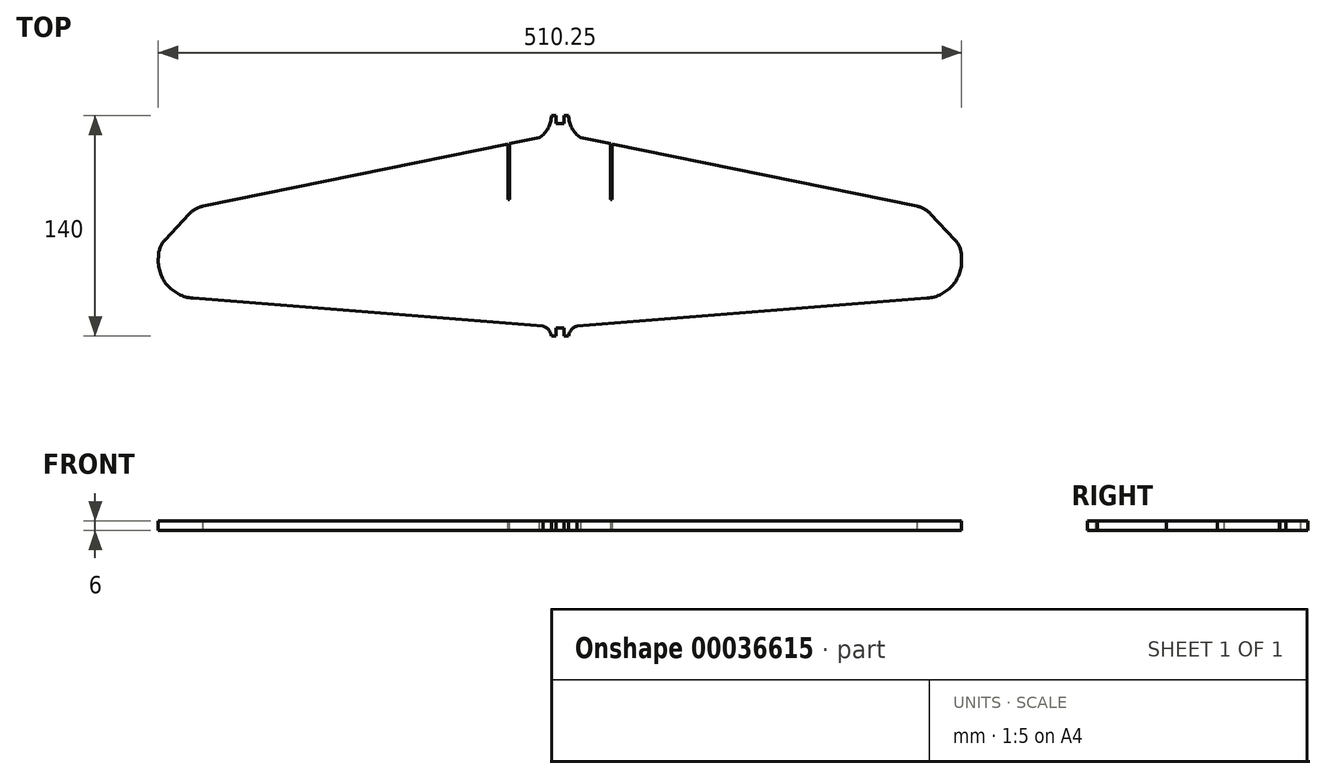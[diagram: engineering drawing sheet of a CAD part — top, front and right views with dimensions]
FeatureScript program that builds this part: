
annotation { "Feature Type Name" : "Feature", "Feature Type Description" : "" }
export const myFeature = defineFeature(function(context is Context, id is Id, definition is map)
    precondition{}
    {
        {
            var Q0;
            Q0=qCreatedBy(makeId("Top.planeOp"),FACE);
            var sketch = newSketch(context, id + "F0", { "sketchPlane" : qUnion([Q0])});
            skLineSegment(sketch, "E0", {"start": v(-57.17, -18.86) * mm, "end": v(-57.17, -69.04) * mm});
            skLineSegment(sketch, "E1", {"start": v(-57.17, -18.86) * mm, "end": v(-57.17, 70.96) * mm});
            skLineSegment(sketch, "E2", {"start": v(-51.78, -62.82) * mm, "end": v(170.5, -45.05) * mm});
            skArc(sketch, "E3", {"start": v(-51.78, -62.82) * mm, "mid": v(-55.43, -65.1) * mm, "end": v(-57.17, -69.04) * mm});
            skArc(sketch, "E4", {"start": v(170.5, -45.05) * mm, "mid": v(186.92, -36.55) * mm, "end": v(192.33, -18.86) * mm});
            skLineSegment(sketch, "E5", {"start": v(-49.68, 56.96) * mm, "end": v(163.94, 13.41) * mm});
            skLineSegment(sketch, "E6", {"start": v(172.75, 8.43) * mm, "end": v(188.16, -7.97) * mm});
            skArc(sketch, "E7", {"start": v(172.75, 8.43) * mm, "mid": v(168.72, 11.59) * mm, "end": v(163.94, 13.41) * mm});
            skArc(sketch, "E8", {"start": v(192.33, -18.86) * mm, "mid": v(191.32, -13) * mm, "end": v(188.16, -7.97) * mm});
            skArc(sketch, "E9", {"start": v(-57.17, 70.96) * mm, "mid": v(-55.18, 63.02) * mm, "end": v(-49.68, 56.96) * mm});
            skLineSegment(sketch, "E10.bottom", {"start": v(-57.17, 70.96) * mm, "end": v(-60.17, 70.96) * mm});
            skLineSegment(sketch, "E10.top", {"start": v(-57.17, -69.04) * mm, "end": v(-60.17, -69.04) * mm});
            skLineSegment(sketch, "E10.left", {"start": v(-57.17, 70.96) * mm, "end": v(-57.17, -69.04) * mm});
            skLineSegment(sketch, "E11", {"start": v(-60.17, 70.96) * mm, "end": v(-60.17, 65.96) * mm});
            skLineSegment(sketch, "E12", {"start": v(-60.17, -69.04) * mm, "end": v(-60.17, -64.04) * mm});
            skLineSegment(sketch, "E13.bottom", {"start": v(-60.17, 65.96) * mm, "end": v(-62.67, 65.96) * mm});
            skLineSegment(sketch, "E13.top", {"start": v(-60.17, -64.04) * mm, "end": v(-62.67, -64.04) * mm});
            skLineSegment(sketch, "E13.left", {"start": v(-60.17, 65.96) * mm, "end": v(-60.17, -64.04) * mm});
            skLineSegment(sketch, "E13.right", {"start": v(-62.67, 65.96) * mm, "end": v(-62.67, -64.04) * mm});
            skLineSegment(sketch, "E14", {"start": v(192.33, -18.86) * mm, "end": v(-62.67, -18.86) * mm});
            skLineSegment(sketch, "E15.top", {"start": v(-30.64, 17.6) * mm, "end": v(-29.64, 17.6) * mm});
            skLineSegment(sketch, "E15.left", {"start": v(-30.64, 53.08) * mm, "end": v(-30.64, 17.6) * mm});
            skLineSegment(sketch, "E16", {"start": v(-29.64, 17.6) * mm, "end": v(-29.64, 52.87) * mm});
            skLineSegment(sketch, "E17", {"start": v(-29.64, 17.6) * mm, "end": v(188.16, -7.97) * mm});
            skSolve(sketch);
        }
        {
            var Q0;
            Q0=makeQuery(id+"F0.imprint","IMPRINT",FACE,{"disambiguationData":[TD([[makeQuery(id+"F0.imprint","IMPRINT",EDGE,{"derivedFrom":sQuery(id+"F0.wireOp",EDGE,"E2")}),1.0]])]});
            var Q1;
            {var subQ6=sQuery(id+"F0.wireOp",EDGE,"E10.bottom");Q1=makeQuery(id+"F0.imprint","IMPRINT",FACE,{"disambiguationData":[TD([[makeQuery(id+"F0.imprint","IMPRINT",EDGE,{"derivedFrom":subQ6}),1.0]])]});}
            var Q2;
            {var subQ5=sQuery(id+"F0.wireOp",EDGE,"E13.bottom");Q2=makeQuery(id+"F0.imprint","IMPRINT",FACE,{"disambiguationData":[TD([[makeQuery(id+"F0.imprint","IMPRINT",EDGE,{"derivedFrom":subQ5}),1.0]])]});}
            var Q3;
            {var subQ6=sQuery(id+"F0.wireOp",EDGE,"E10.top");Q3=makeQuery(id+"F0.imprint","IMPRINT",FACE,{"disambiguationData":[TD([[makeQuery(id+"F0.imprint","IMPRINT",EDGE,{"derivedFrom":subQ6}),-1.0]])]});}
            var Q4;
            {var subQ3=sQuery(id+"F0.wireOp",EDGE,"E13.top");Q4=makeQuery(id+"F0.imprint","IMPRINT",FACE,{"disambiguationData":[TD([[makeQuery(id+"F0.imprint","IMPRINT",EDGE,{"derivedFrom":subQ3}),-1.0]])]});}
            var Q5;
            {var subQ5=sQuery(id+"F0.wireOp",EDGE,"E8");Q5=makeQuery(id+"F0.imprint","IMPRINT",FACE,{"disambiguationData":[TD([[makeQuery(id+"F0.imprint","IMPRINT",EDGE,{"derivedFrom":subQ5}),1.0]])]});}
            var Q6;
            Q6=makeQuery(id+"F0.imprint","IMPRINT",FACE,{"disambiguationData":[TD([[makeQuery(id+"F0.imprint","IMPRINT",EDGE,{"derivedFrom":sQuery(id+"F0.wireOp",EDGE,"E6")}),-1.0]])]});
            extrude(context, id + "F1", {"entities" : qUnion([Q0, Q1, Q2, Q3, Q4, Q5, Q6]), "depth" : 6 * mm});
        }
        {
            var Q0;
            Q0=makeQuery(id+"F1.opExtrude","SWEPT_FACE",FACE,{"disambiguationData":[OSD([sQuery(id+"F0.wireOp",EDGE,"E13.right")])]});
            var sketch = newSketch(context, id + "F2", { "sketchPlane" : qUnion([Q0])});
            skLineSegment(sketch, "E18", {"start": v(-65.96, 3) * mm, "end": v(64.04, 3) * mm});
            skSolve(sketch);
        }
        {
            var Q0;
            Q0=makeQuery(id+"F1.opExtrude","SWEPT_BODY",BODY,{"disambiguationData":[OSD([sQuery(id+"F0.wireOp",EDGE,"E2"),sQuery(id+"F0.wireOp",EDGE,"E3"),sQuery(id+"F0.wireOp",EDGE,"E4"),sQuery(id+"F0.wireOp",EDGE,"E5"),sQuery(id+"F0.wireOp",EDGE,"E6"),sQuery(id+"F0.wireOp",EDGE,"E7"),sQuery(id+"F0.wireOp",EDGE,"E8"),sQuery(id+"F0.wireOp",EDGE,"E9"),sQuery(id+"F0.wireOp",EDGE,"E10.bottom"),sQuery(id+"F0.wireOp",EDGE,"E10.top"),sQuery(id+"F0.wireOp",EDGE,"E11"),sQuery(id+"F0.wireOp",EDGE,"E12"),sQuery(id+"F0.wireOp",EDGE,"E13.bottom"),sQuery(id+"F0.wireOp",EDGE,"E13.top"),sQuery(id+"F0.wireOp",EDGE,"E13.right")])]});
            var Q1;
            Q1=sQuery(id+"F2.wireOp",EDGE,"E18");
            circularPattern(context, id + "F3", {"operationType" : NewBodyOperationType.ADD, "entities" : qUnion([Q0]), "axis" : qUnion([Q1]), "angle" : 180 * degree, "instanceCount" : 2});
        }
    });
